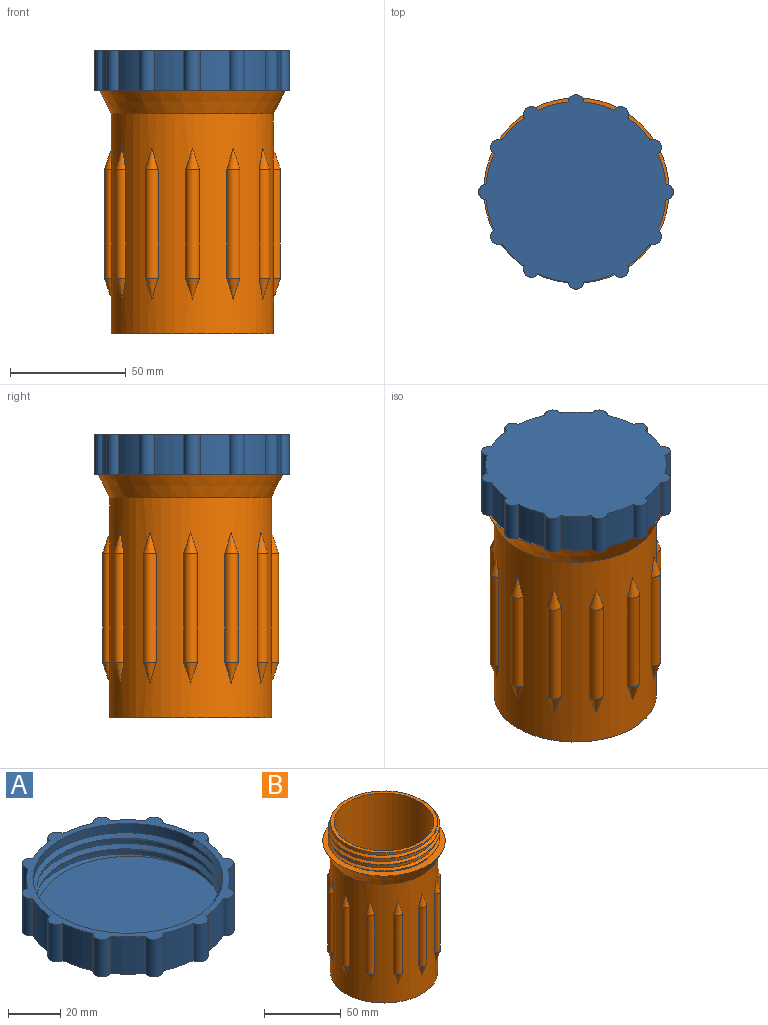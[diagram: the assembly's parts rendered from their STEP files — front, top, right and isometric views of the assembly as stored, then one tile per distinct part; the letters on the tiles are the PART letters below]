
ASSEMBLY  parts=2 mates=1
PART A: 31 faces, bbox 84.9x85.2x18.4 mm
  f0: cylinder r=39mm len=17.5mm, axis (0,0,-1), area 235.3mm2, adj f14,f15,f19,f30
  f1: cylinder r=39mm len=17.5mm, axis (0,0,-1), area 235.3mm2, adj f14,f15,f29,f30
  f2: cylinder r=39mm len=17.5mm, axis (0,0,-1), area 235.3mm2, adj f14,f15,f28,f29
  f3: cylinder r=39mm len=17.5mm, axis (0,0,-1), area 235.3mm2, adj f14,f15,f27,f28
  f4: cylinder r=39mm len=17.5mm, axis (0,0,-1), area 235.3mm2, adj f14,f15,f26,f27
  f5: cylinder r=39mm len=17.5mm, axis (0,0,-1), area 235.3mm2, adj f14,f15,f25,f26
  f6: cylinder r=39mm len=17.5mm, axis (0,0,-1), area 235.3mm2, adj f14,f15,f24,f25
  f7: cylinder r=39mm len=17.5mm, axis (0,0,-1), area 235.3mm2, adj f14,f15,f23,f24
  f8: cylinder r=39mm len=17.5mm, axis (0,0,-1), area 235.3mm2, adj f14,f15,f22,f23
  f9: cylinder r=39mm len=17.5mm, axis (0,0,-1), area 235.3mm2, adj f14,f15,f21,f22
  f10: cylinder r=39mm len=17.5mm, axis (0,0,-1), area 235.3mm2, adj f14,f15,f20,f21
  f11: cylinder r=36.5mm len=73mm, axis (0,0,-1), area 1584.1mm2, adj f12,f14,f16,f17,f18
  f12: plane 73.41x72.65mm, normal (0,0,1), area 4083.5mm2, adj f11,f17,f18
  f13: cylinder r=39mm len=17.5mm, axis (0,0,-1), area 235.3mm2, adj f14,f15,f19,f20
  f14: plane 84x84mm, normal (0,0,1), area 786.3mm2, adj f0,f1,f2,f3,f4,f5,f6,f7
  f15: plane 84x84mm, normal (0,0,-1), area 4971.7mm2, adj f0,f1,f2,f3,f4,f5,f6,f7
  f16: plane 3x1.5mm, normal (0,1,0.02), area 2.3mm2, adj f11,f17,f18
  f17: bspline ~72.99x72.75mm, area 1214.3mm2, adj f11,f12,f16,f18
  f18: bspline ~84.29x73mm, area 1359.8mm2, adj f11,f12,f16,f17
  f19: cylinder r=3.5mm len=17.5mm, axis (0,0,1), area 180.4mm2, adj f0,f13,f14,f15
  f20: cylinder r=3.5mm len=17.5mm, axis (0,0,1), area 180.4mm2, adj f10,f13,f14,f15
  f21: cylinder r=3.5mm len=17.5mm, axis (0,0,1), area 180.4mm2, adj f9,f10,f14,f15
  f22: cylinder r=3.5mm len=17.5mm, axis (0,0,1), area 180.4mm2, adj f8,f9,f14,f15
  f23: cylinder r=3.5mm len=17.5mm, axis (0,0,1), area 180.4mm2, adj f7,f8,f14,f15
  f24: cylinder r=3.5mm len=17.5mm, axis (0,0,1), area 180.4mm2, adj f6,f7,f14,f15
  f25: cylinder r=3.5mm len=17.5mm, axis (0,0,1), area 180.4mm2, adj f5,f6,f14,f15
  f26: cylinder r=3.5mm len=17.5mm, axis (0,0,1), area 180.4mm2, adj f4,f5,f14,f15
  f27: cylinder r=3.5mm len=17.5mm, axis (0,0,1), area 180.4mm2, adj f3,f4,f14,f15
  f28: cylinder r=3.5mm len=17.5mm, axis (0,0,1), area 180.4mm2, adj f2,f3,f14,f15
  f29: cylinder r=3.5mm len=17.5mm, axis (0,0,1), area 180.4mm2, adj f1,f2,f14,f15
  f30: cylinder r=3.5mm len=17.5mm, axis (0,0,1), area 180.4mm2, adj f0,f1,f14,f15
PART B: 79 faces, bbox 81.2x85.5x121.2 mm
  f0: cylinder r=35mm len=70mm, axis (0,0,-1), area 1636.8mm2, adj f1,f4,f5,f77,f78
  f1: plane 70x70mm, normal (0,0,1), area 530.1mm2, adj f0,f2
  f2: cylinder r=32.5mm len=117.5mm, axis (0,0,-1), area 23993.9mm2, adj f1,f3
  f3: plane 65x65mm, normal (0,0,1), area 3318.3mm2, adj f2
  f4: bspline ~84.29x73.04mm, area 1358.6mm2, adj f0,f5,f77,f78
  f5: plane 81.2x81.2mm, normal (0,0,1), area 1077.8mm2, adj f0,f4,f6,f77
  f6: cone r=35mm half-angle=26.6deg, axis (0,0,1), area 2634.3mm2, adj f5,f7
  f7: cylinder r=35mm len=95mm, axis (0,0,-1), area 18713.4mm2, adj f6,f8,f10,f11,f12,f13,f15,f16
  f8: plane 56x1.5mm, normal (1,-0.02,0), area 77.2mm2, adj f7,f9,f10,f12
  f9: cylinder r=3mm len=47mm, axis (0,0,1), area 449mm2, adj f8,f10,f11,f12
  f10: cone r=3mm half-angle=18.4deg, axis (0,0,1), area 41.5mm2, adj f7,f8,f9,f11
  f11: plane 56x1.5mm, normal (1,0.02,0), area 77.2mm2, adj f7,f9,f10,f12
  f12: cone r=0mm half-angle=18.4deg, axis (0,0,-1), area 41.5mm2, adj f7,f8,f9,f11
  f13: plane 56x1.28mm, normal (0.86,-0.52,0), area 77.3mm2, adj f7,f14,f15,f18
  f14: cylinder r=3mm len=47mm, axis (0,0,1), area 449mm2, adj f13,f15,f17,f18
  f15: cone r=3mm half-angle=18.4deg, axis (0,0,1), area 37.4mm2, adj f7,f13,f14,f17
  f16: cone r=3mm half-angle=18.4deg, axis (0,0,1), area 3.3mm2, adj f7
  f17: plane 56x1.32mm, normal (0.88,-0.48,0), area 77.3mm2, adj f7,f14,f15,f18
  f18: cone r=0mm half-angle=18.4deg, axis (0,0,-1), area 41.5mm2, adj f7,f13,f14,f17
  f19: plane 56x1.32mm, normal (0.48,-0.88,0), area 77.3mm2, adj f7,f20,f21,f24
  f20: cylinder r=3mm len=47mm, axis (0,0,1), area 449mm2, adj f19,f21,f23,f24
  f21: cone r=3mm half-angle=18.4deg, axis (0,0,1), area 37.4mm2, adj f7,f19,f20,f23
  f22: cone r=3mm half-angle=18.4deg, axis (0,0,1), area 3.3mm2, adj f7
  f23: plane 56x1.28mm, normal (0.52,-0.86,0), area 77.3mm2, adj f7,f20,f21,f24
  f24: cone r=0mm half-angle=18.4deg, axis (0,0,-1), area 41.5mm2, adj f7,f19,f20,f23
  f25: plane 56x1.5mm, normal (-0.02,-1,0), area 77.2mm2, adj f7,f26,f27,f29
  f26: cylinder r=3mm len=47mm, axis (0,0,1), area 449mm2, adj f25,f27,f28,f29
  f27: cone r=3mm half-angle=18.4deg, axis (0,0,1), area 41.5mm2, adj f7,f25,f26,f28
  f28: plane 56x1.5mm, normal (0.02,-1,0), area 77.2mm2, adj f7,f26,f27,f29
  f29: cone r=0mm half-angle=18.4deg, axis (0,0,-1), area 41.5mm2, adj f7,f25,f26,f28
  f30: plane 56x1.28mm, normal (-0.52,-0.86,0), area 77.3mm2, adj f7,f31,f32,f35
  f31: cylinder r=3mm len=47mm, axis (0,0,1), area 449mm2, adj f30,f32,f34,f35
  f32: cone r=3mm half-angle=18.4deg, axis (0,0,1), area 37.4mm2, adj f7,f30,f31,f34
  f33: cone r=3mm half-angle=18.4deg, axis (0,0,1), area 3.3mm2, adj f7
  f34: plane 56x1.32mm, normal (-0.48,-0.88,0), area 77.3mm2, adj f7,f31,f32,f35
  f35: cone r=0mm half-angle=18.4deg, axis (0,0,-1), area 41.5mm2, adj f7,f30,f31,f34
  f36: plane 56x1.32mm, normal (-0.88,-0.48,0), area 77.3mm2, adj f7,f37,f38,f41
  f37: cylinder r=3mm len=47mm, axis (0,0,1), area 449mm2, adj f36,f38,f40,f41
  f38: cone r=3mm half-angle=18.4deg, axis (0,0,1), area 37.4mm2, adj f7,f36,f37,f40
  f39: cone r=3mm half-angle=18.4deg, axis (0,0,1), area 3.3mm2, adj f7
  f40: plane 56x1.28mm, normal (-0.86,-0.52,0), area 77.3mm2, adj f7,f37,f38,f41
  f41: cone r=0mm half-angle=18.4deg, axis (0,0,-1), area 41.5mm2, adj f7,f36,f37,f40
  f42: plane 56x1.28mm, normal (-0.86,0.52,0), area 77.3mm2, adj f7,f43,f44,f47
  f43: cylinder r=3mm len=47mm, axis (0,0,1), area 449mm2, adj f42,f44,f46,f47
  f44: cone r=3mm half-angle=18.4deg, axis (0,0,1), area 37.4mm2, adj f7,f42,f43,f46
  f45: cone r=3mm half-angle=18.4deg, axis (0,0,1), area 3.3mm2, adj f7
  f46: plane 56x1.32mm, normal (-0.88,0.48,0), area 77.3mm2, adj f7,f43,f44,f47
  f47: cone r=0mm half-angle=18.4deg, axis (0,0,-1), area 41.5mm2, adj f7,f42,f43,f46
  f48: plane 56x1.32mm, normal (-0.48,0.88,0), area 77.3mm2, adj f7,f49,f50,f53
  f49: cylinder r=3mm len=47mm, axis (0,0,1), area 449mm2, adj f48,f50,f52,f53
  f50: cone r=3mm half-angle=18.4deg, axis (0,0,1), area 37.4mm2, adj f7,f48,f49,f52
  f51: cone r=3mm half-angle=18.4deg, axis (0,0,1), area 3.3mm2, adj f7
  f52: plane 56x1.28mm, normal (-0.52,0.86,0), area 77.3mm2, adj f7,f49,f50,f53
  f53: cone r=0mm half-angle=18.4deg, axis (0,0,-1), area 41.5mm2, adj f7,f48,f49,f52
  f54: plane 56x1.5mm, normal (0.02,1,0), area 77.2mm2, adj f7,f55,f56,f58
  f55: cylinder r=3mm len=47mm, axis (0,0,1), area 449mm2, adj f54,f56,f57,f58
  f56: cone r=3mm half-angle=18.4deg, axis (0,0,1), area 41.5mm2, adj f7,f54,f55,f57
  f57: plane 56x1.5mm, normal (-0.02,1,0), area 77.2mm2, adj f7,f55,f56,f58
  f58: cone r=0mm half-angle=18.4deg, axis (0,0,-1), area 41.5mm2, adj f7,f54,f55,f57
  f59: plane 56x1.28mm, normal (0.52,0.86,0), area 77.3mm2, adj f7,f60,f61,f64
  f60: cylinder r=3mm len=47mm, axis (0,0,1), area 449mm2, adj f59,f61,f63,f64
  f61: cone r=3mm half-angle=18.4deg, axis (0,0,1), area 37.4mm2, adj f7,f59,f60,f63
  f62: cone r=3mm half-angle=18.4deg, axis (0,0,1), area 3.3mm2, adj f7
  f63: plane 56x1.32mm, normal (0.48,0.88,0), area 77.3mm2, adj f7,f60,f61,f64
  f64: cone r=0mm half-angle=18.4deg, axis (0,0,-1), area 41.5mm2, adj f7,f59,f60,f63
  f65: plane 56x1.32mm, normal (0.88,0.48,0), area 77.3mm2, adj f7,f66,f67,f70
  f66: cylinder r=3mm len=47mm, axis (0,0,1), area 449mm2, adj f65,f67,f69,f70
  f67: cone r=3mm half-angle=18.4deg, axis (0,0,1), area 37.4mm2, adj f7,f65,f66,f69
  f68: cone r=3mm half-angle=18.4deg, axis (0,0,1), area 3.3mm2, adj f7
  f69: plane 56x1.28mm, normal (0.86,0.52,0), area 77.3mm2, adj f7,f66,f67,f70
  f70: cone r=0mm half-angle=18.4deg, axis (0,0,-1), area 41.5mm2, adj f7,f65,f66,f69
  f71: plane 56x1.5mm, normal (-1,0.02,0), area 77.2mm2, adj f7,f72,f74,f76
  f72: cylinder r=3mm len=47mm, axis (0,0,1), area 449mm2, adj f71,f74,f75,f76
  f73: plane 70x70mm, normal (0,0,-1), area 3848.5mm2, adj f7
  f74: cone r=3mm half-angle=18.4deg, axis (0,0,1), area 41.5mm2, adj f7,f71,f72,f75
  f75: plane 56x1.5mm, normal (-1,-0.02,0), area 77.2mm2, adj f7,f72,f74,f76
  f76: cone r=0mm half-angle=18.4deg, axis (0,0,-1), area 41.5mm2, adj f7,f71,f72,f75
  f77: bspline ~84.29x73.04mm, area 1216.3mm2, adj f0,f4,f5,f78
  f78: plane 3x1.5mm, normal (0,1,0.02), area 2.2mm2, adj f0,f4,f77
PLACE A rot(axis=(-1,0,0),180deg) t=(-0.2,-0.63,122.5)mm
PLACE B rot(axis=(0,0,1),180deg) t=(0,0,0)mm
MATE cylindrical B.f0 <-> A.f12  axis (0,0,1) through (0,0,120)mm
